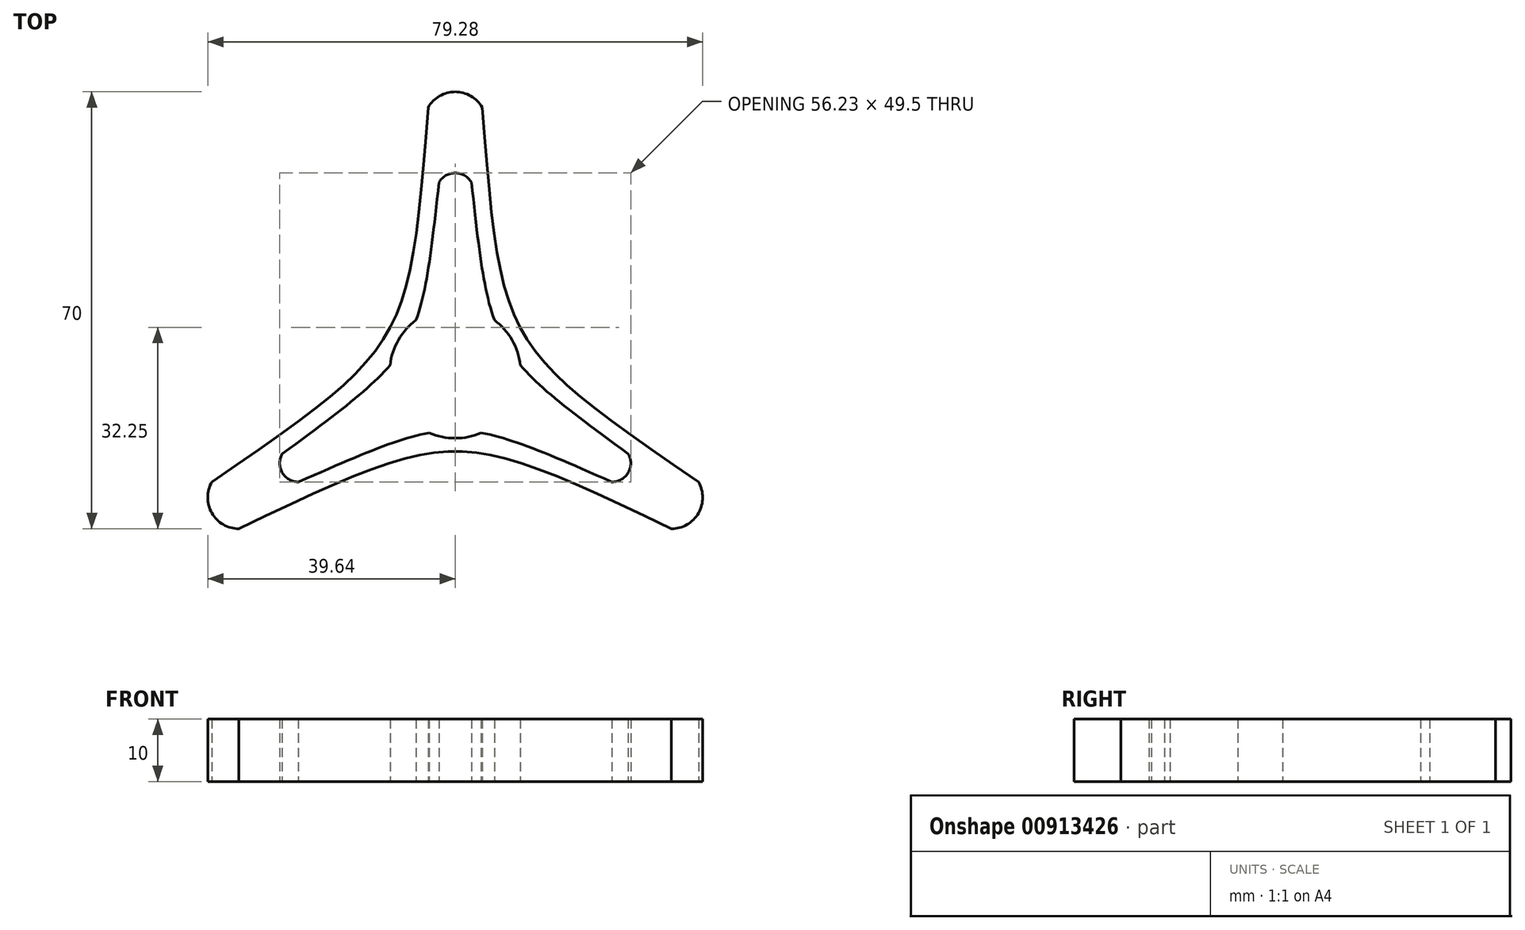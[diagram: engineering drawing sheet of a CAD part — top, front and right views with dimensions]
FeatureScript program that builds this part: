
annotation { "Feature Type Name" : "Feature", "Feature Type Description" : "" }
export const myFeature = defineFeature(function(context is Context, id is Id, definition is map)
    precondition{}
    {
        {
            var Q0;
            Q0=qCreatedBy(makeId("Top.planeOp"),FACE);
            var sketch = newSketch(context, id + "F0", { "sketchPlane" : qUnion([Q0])});
            skArc(sketch, "E0", {"start": v(-6.27, 8.42) * mm, "mid": v(-9.1, 5.25) * mm, "end": v(-10.43, 1.22) * mm});
            skPoint(sketch, "E1.cCircle.perimeterSnap0", {"position": v(0, 5.25) * mm});
            skPoint(sketch, "E1.0.startSnap0", {"position": v(0, 5.25) * mm});
            skPoint(sketch, "E2.visualSharp", {"position": v(0, 50) * mm});
            skArc(sketch, "E2.filletArc", {"start": v(4.33, 42.5) * mm, "mid": v(0, 45) * mm, "end": v(-4.33, 42.5) * mm});
            skPoint(sketch, "E3.visualSharp", {"position": v(43.3, -25) * mm});
            skArc(sketch, "E3.filletArc", {"start": v(34.64, -25) * mm, "mid": v(38.97, -22.5) * mm, "end": v(38.97, -17.5) * mm});
            skPoint(sketch, "E4.visualSharp", {"position": v(-43.3, -25) * mm});
            skArc(sketch, "E4.filletArc", {"start": v(-38.97, -17.5) * mm, "mid": v(-38.97, -22.5) * mm, "end": v(-34.64, -25) * mm});
            skPoint(sketch, "E5.visualSharp", {"position": v(0, 35) * mm});
            skArc(sketch, "E5.filletArc", {"start": v(2.6, 30.5) * mm, "mid": v(0, 32) * mm, "end": v(-2.6, 30.5) * mm});
            skPoint(sketch, "E6.visualSharp", {"position": v(30.31, -17.5) * mm});
            skArc(sketch, "E6.filletArc", {"start": v(25.11, -17.5) * mm, "mid": v(27.71, -16) * mm, "end": v(27.71, -13) * mm});
            skPoint(sketch, "E7.visualSharp", {"position": v(-30.31, -17.5) * mm});
            skArc(sketch, "E7.filletArc", {"start": v(-27.71, -13) * mm, "mid": v(-27.71, -16) * mm, "end": v(-25.11, -17.5) * mm});
            skFitSpline(sketch, "E8", {"points": [v(2.6, 30.5) * mm, v(27.71, -13) * mm], "startDerivative": vector(9.1, -81.75) * mm, "endDerivative": vector(66.25, -48.75) * mm});
            skFitSpline(sketch, "E9", {"points": [v(4.33, 42.5) * mm, v(38.97, -17.5) * mm], "startDerivative": vector(9.1, -114.75) * mm, "endDerivative": vector(94.83, -65.25) * mm});
            skFitSpline(sketch, "E10", {"points": [v(25.11, -17.5) * mm, v(-25.11, -17.5) * mm], "startDerivative": vector(-75.34, 33) * mm, "endDerivative": vector(-75.34, -33) * mm});
            skFitSpline(sketch, "E11", {"points": [v(-34.64, -25) * mm, v(34.64, -25) * mm], "startDerivative": vector(103.92, 49.5) * mm, "endDerivative": vector(103.92, -49.5) * mm});
            skFitSpline(sketch, "E12", {"points": [v(-38.97, -17.5) * mm, v(-4.33, 42.5) * mm], "startDerivative": vector(94.83, 65.25) * mm, "endDerivative": vector(9.1, 114.75) * mm});
            skFitSpline(sketch, "E13", {"points": [v(-2.6, 30.5) * mm, v(-27.71, -13) * mm], "startDerivative": vector(-9.1, -81.75) * mm, "endDerivative": vector(-66.25, -48.75) * mm});
            skFitSpline(sketch, "E14.trimOffspring", {"points": [v(-2.6, 30.5) * mm, v(-27.71, -13) * mm], "startDerivative": vector(-9.1, -81.75) * mm, "endDerivative": vector(-66.25, -48.75) * mm});
            skFitSpline(sketch, "E15.trimOffspring", {"points": [v(2.6, 30.5) * mm, v(27.71, -13) * mm], "startDerivative": vector(9.1, -81.75) * mm, "endDerivative": vector(66.25, -48.75) * mm});
            skArc(sketch, "E16.trimOffspring", {"start": v(10.43, 1.22) * mm, "mid": v(9.1, 5.25) * mm, "end": v(6.27, 8.42) * mm});
            skFitSpline(sketch, "E17.trimOffspring", {"points": [v(25.11, -17.5) * mm, v(-25.11, -17.5) * mm], "startDerivative": vector(-75.34, 33) * mm, "endDerivative": vector(-75.34, -33) * mm});
            skArc(sketch, "E18.trimOffspring", {"start": v(-4.16, -9.64) * mm, "mid": v(0, -10.5) * mm, "end": v(4.16, -9.64) * mm});
            skSolve(sketch);
        }
        {
            var Q0;
            Q0=makeQuery(id+"F0.imprint","IMPRINT",FACE,{"disambiguationData":[TD([[makeQuery(id+"F0.imprint","IMPRINT",EDGE,{"derivedFrom":sQuery(id+"F0.wireOp",EDGE,"E0")}),-1.0]])]});
            extrude(context, id + "F1", {"entities" : qUnion([Q0]), "depth" : 10 * mm, "offsetDistance" : 25 * mm});
        }
    });
